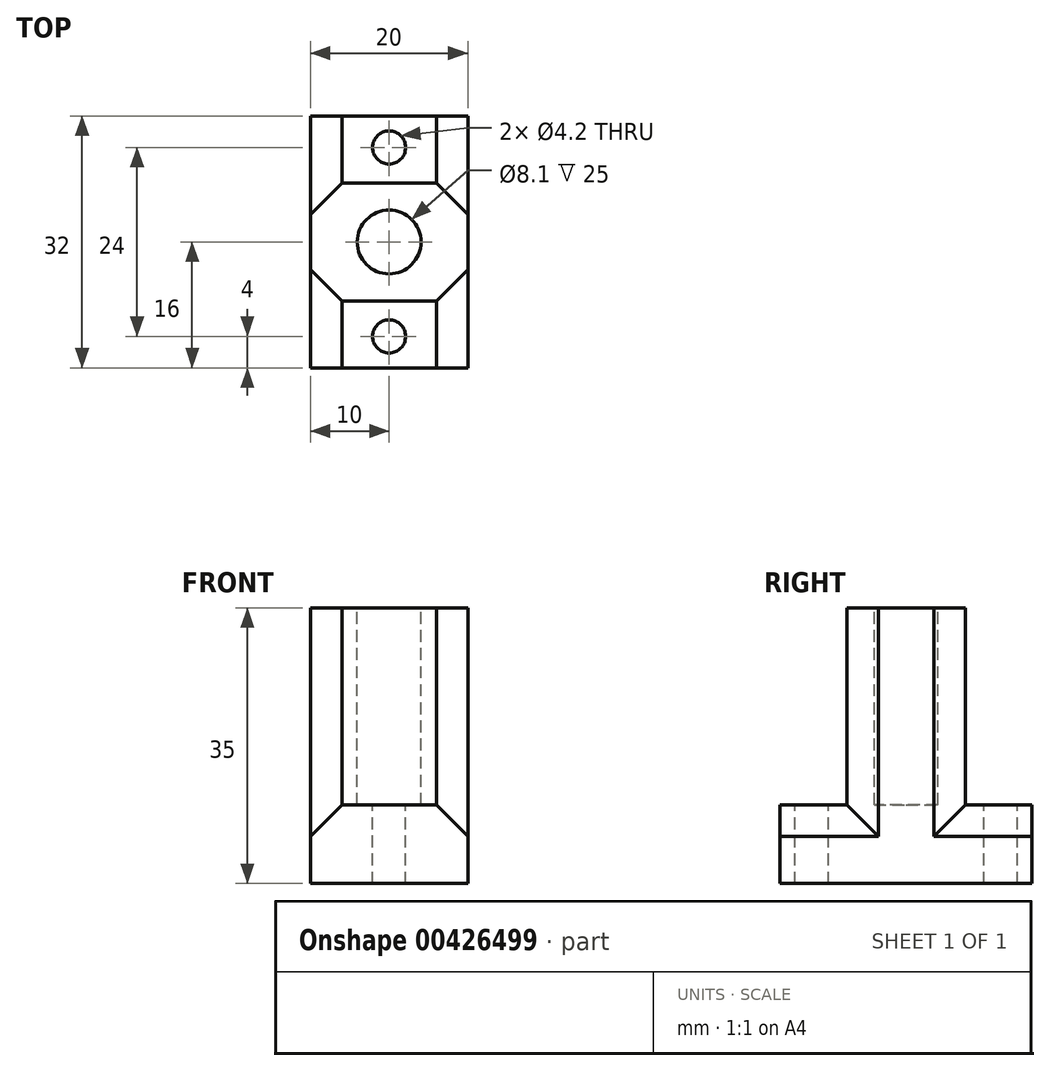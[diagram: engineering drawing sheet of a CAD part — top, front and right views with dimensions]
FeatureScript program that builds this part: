
annotation { "Feature Type Name" : "Feature", "Feature Type Description" : "" }
export const myFeature = defineFeature(function(context is Context, id is Id, definition is map)
    precondition{}
    {
        {
            var Q0;
            Q0=qCreatedBy(makeId("Top.planeOp"),FACE);
            var sketch = newSketch(context, id + "F0", { "sketchPlane" : qUnion([Q0])});
            skLineSegment(sketch, "E0", {"start": v(0, 0) * mm, "end": v(0, 16) * mm, "construction": true});
            skLineSegment(sketch, "E1", {"start": v(0, 0) * mm, "end": v(-10, 0) * mm, "construction": true});
            skLineSegment(sketch, "E2", {"start": v(-10, 0) * mm, "end": v(-10, -16) * mm});
            skLineSegment(sketch, "E3", {"start": v(-10, -16) * mm, "end": v(0, -16) * mm});
            skLineSegment(sketch, "E4", {"start": v(0, -16) * mm, "end": v(0, 0) * mm, "construction": true});
            skLineSegment(sketch, "E5", {"start": v(0, 0) * mm, "end": v(10, 0) * mm, "construction": true});
            skLineSegment(sketch, "E6", {"start": v(10, 0) * mm, "end": v(10, -16) * mm});
            skLineSegment(sketch, "E7", {"start": v(10, -16) * mm, "end": v(0, -16) * mm});
            skLineSegment(sketch, "E8", {"start": v(0, 16) * mm, "end": v(10, 16) * mm});
            skLineSegment(sketch, "E9", {"start": v(10, 16) * mm, "end": v(10, 0) * mm});
            skLineSegment(sketch, "E10", {"start": v(0, 16) * mm, "end": v(-10, 16) * mm});
            skLineSegment(sketch, "E11", {"start": v(-10, 16) * mm, "end": v(-10, 0) * mm});
            skSolve(sketch);
        }
        {
            var Q0;
            Q0 = qSketchRegion(id + "F0", true);
            extrude(context, id + "F1", {"entities" : qUnion([Q0]), "depth" : 10 * mm});
        }
        {
            var Q0;
            Q0=makeQuery(id+"F1.opExtrude","CAP_FACE",FACE,{"disambiguationData":[OSD([sQuery(id+"F0.wireOp",EDGE,"E2"),sQuery(id+"F0.wireOp",EDGE,"E3"),sQuery(id+"F0.wireOp",EDGE,"E6"),sQuery(id+"F0.wireOp",EDGE,"E7"),sQuery(id+"F0.wireOp",EDGE,"E8"),sQuery(id+"F0.wireOp",EDGE,"E9"),sQuery(id+"F0.wireOp",EDGE,"E10"),sQuery(id+"F0.wireOp",EDGE,"E11")])],"isStart":false});
            var sketch = newSketch(context, id + "F2", { "sketchPlane" : qUnion([Q0])});
            skLineSegment(sketch, "E12", {"start": v(0, 0) * mm, "end": v(0, 7.5) * mm, "construction": true});
            skLineSegment(sketch, "E13", {"start": v(0, 7.5) * mm, "end": v(10, 7.5) * mm});
            skLineSegment(sketch, "E14", {"start": v(10, 7.5) * mm, "end": v(10, 0) * mm});
            skLineSegment(sketch, "E15", {"start": v(10, 0) * mm, "end": v(0, 0) * mm, "construction": true});
            skLineSegment(sketch, "E16", {"start": v(0, 0) * mm, "end": v(0, -7.5) * mm, "construction": true});
            skLineSegment(sketch, "E17", {"start": v(0, -7.5) * mm, "end": v(10, -7.5) * mm});
            skLineSegment(sketch, "E18", {"start": v(10, -7.5) * mm, "end": v(10, 0) * mm});
            skLineSegment(sketch, "E19", {"start": v(0, -7.5) * mm, "end": v(-10, -7.5) * mm});
            skLineSegment(sketch, "E20", {"start": v(-10, -7.5) * mm, "end": v(-10, 7.5) * mm});
            skLineSegment(sketch, "E21", {"start": v(-10, 7.5) * mm, "end": v(0, 7.5) * mm});
            skLineSegment(sketch, "E22", {"start": v(0, 0) * mm, "end": v(-10, 0) * mm, "construction": true});
            skSolve(sketch);
        }
        {
            var Q0;
            Q0 = qSketchRegion(id + "F2", true);
            extrude(context, id + "F3", {"entities" : qUnion([Q0]), "operationType" : NewBodyOperationType.ADD, "depth" : 25 * mm});
        }
        {
            var Q0;
            Q0=makeQuery(id+"F3.opExtrude","SWEPT_EDGE",EDGE,{"disambiguationData":[OSD([sQuery(id+"F0.wireOp",EDGE,"E2"),sQuery(id+"F0.wireOp",EDGE,"E11"),sQuery(id+"F2.wireOp",EDGE,"E19"),sQuery(id+"F2.wireOp",EDGE,"E20")])]});
            var Q1;
            Q1=makeQuery(id+"F3.opExtrude","SWEPT_EDGE",EDGE,{"disambiguationData":[OSD([sQuery(id+"F0.wireOp",EDGE,"E6"),sQuery(id+"F0.wireOp",EDGE,"E9"),sQuery(id+"F2.wireOp",EDGE,"E17"),sQuery(id+"F2.wireOp",EDGE,"E18")])]});
            var Q2;
            Q2=makeQuery(id+"F3.opExtrude","SWEPT_EDGE",EDGE,{"disambiguationData":[OSD([sQuery(id+"F0.wireOp",EDGE,"E6"),sQuery(id+"F0.wireOp",EDGE,"E9"),sQuery(id+"F2.wireOp",EDGE,"E13"),sQuery(id+"F2.wireOp",EDGE,"E14")])]});
            var Q3;
            Q3=makeQuery(id+"F3.opExtrude","SWEPT_EDGE",EDGE,{"disambiguationData":[OSD([sQuery(id+"F0.wireOp",EDGE,"E2"),sQuery(id+"F0.wireOp",EDGE,"E11"),sQuery(id+"F2.wireOp",EDGE,"E20"),sQuery(id+"F2.wireOp",EDGE,"E21")])]});
            chamfer(context, id + "F4", {"entities" : qUnion([Q0, Q1, Q2, Q3]), "width" : 4 * mm, "tangentPropagation" : true});
        }
        {
            var Q0;
            {var subQ0=sQuery(id+"F0.wireOp",EDGE,"E10");var subQ1=sQuery(id+"F0.wireOp",EDGE,"E8");var subQ2=sQuery(id+"F0.wireOp",EDGE,"E9");var subQ3=sQuery(id+"F0.wireOp",EDGE,"E6");var subQ4=sQuery(id+"F0.wireOp",EDGE,"E11");var subQ5=sQuery(id+"F0.wireOp",EDGE,"E2");Q0=makeQuery(id+"F3.boolean.opBoolean","SPLIT",FACE,{"disambiguationData":[TD([makeQuery(id+"F1.opExtrude","SWEPT_FACE",FACE,{"disambiguationData":[OSD([subQ1,subQ0])]})])],"derivedFrom":makeQuery(id+"F1.opExtrude","CAP_FACE",FACE,{"disambiguationData":[OSD([subQ5,sQuery(id+"F0.wireOp",EDGE,"E3"),subQ3,sQuery(id+"F0.wireOp",EDGE,"E7"),subQ1,subQ2,subQ0,subQ4])],"isStart":false})});}
            var sketch = newSketch(context, id + "F5", { "sketchPlane" : qUnion([Q0])});
            skCircle(sketch, "E23", {"center": v(0, 12) * mm, "radius": 2.1 * mm});
            skCircle(sketch, "E24", {"center": v(0, -12) * mm, "radius": 2.1 * mm});
            skSolve(sketch);
        }
        {
            var Q0;
            Q0 = qSketchRegion(id + "F5", true);
            extrude(context, id + "F6", {"entities" : qUnion([Q0]), "operationType" : NewBodyOperationType.REMOVE, "endBound" : BoundingType.THROUGH_ALL, "oppositeDirection" : true, "depth" : 25 * mm});
        }
        {
            var Q0;
            Q0=makeQuery(id+"F3.opExtrude","CAP_FACE",FACE,{"disambiguationData":[OSD([sQuery(id+"F2.wireOp",EDGE,"E13"),sQuery(id+"F2.wireOp",EDGE,"E14"),sQuery(id+"F2.wireOp",EDGE,"E17"),sQuery(id+"F2.wireOp",EDGE,"E18"),sQuery(id+"F2.wireOp",EDGE,"E19"),sQuery(id+"F2.wireOp",EDGE,"E20"),sQuery(id+"F2.wireOp",EDGE,"E21")])],"isStart":false});
            var sketch = newSketch(context, id + "F7", { "sketchPlane" : qUnion([Q0])});
            skCircle(sketch, "E25", {"center": v(0, 0) * mm, "radius": 4.05 * mm});
            skSolve(sketch);
        }
        {
            var Q0;
            Q0 = qSketchRegion(id + "F7", true);
            extrude(context, id + "F8", {"entities" : qUnion([Q0]), "operationType" : NewBodyOperationType.REMOVE, "oppositeDirection" : true, "depth" : 25 * mm});
        }
        {
            var Q0;
            {var subQ0=sQuery(id+"F0.wireOp",EDGE,"E10");var subQ1=sQuery(id+"F0.wireOp",EDGE,"E8");var subQ2=sQuery(id+"F0.wireOp",EDGE,"E11");var subQ3=sQuery(id+"F0.wireOp",EDGE,"E2");Q0=makeQuery(id+"F3.boolean.opBoolean","SPLIT",EDGE,{"disambiguationData":[TD([makeQuery(id+"F1.opExtrude","SWEPT_FACE",FACE,{"disambiguationData":[OSD([subQ1,subQ0])]})])],"derivedFrom":makeQuery(id+"F1.opExtrude","CAP_EDGE",EDGE,{"disambiguationData":[OSD([subQ3,subQ2])],"isStart":false})});}
            var Q1;
            {var subQ0=sQuery(id+"F0.wireOp",EDGE,"E7");var subQ1=sQuery(id+"F0.wireOp",EDGE,"E3");var subQ2=sQuery(id+"F0.wireOp",EDGE,"E11");var subQ3=sQuery(id+"F0.wireOp",EDGE,"E2");Q1=makeQuery(id+"F3.boolean.opBoolean","SPLIT",EDGE,{"disambiguationData":[TD([makeQuery(id+"F1.opExtrude","SWEPT_FACE",FACE,{"disambiguationData":[OSD([subQ1,subQ0])]})])],"derivedFrom":makeQuery(id+"F1.opExtrude","CAP_EDGE",EDGE,{"disambiguationData":[OSD([subQ3,subQ2])],"isStart":false})});}
            var Q2;
            {var subQ0=sQuery(id+"F0.wireOp",EDGE,"E9");var subQ1=sQuery(id+"F0.wireOp",EDGE,"E6");var subQ2=sQuery(id+"F0.wireOp",EDGE,"E7");var subQ3=sQuery(id+"F0.wireOp",EDGE,"E3");Q2=makeQuery(id+"F3.boolean.opBoolean","SPLIT",EDGE,{"disambiguationData":[TD([makeQuery(id+"F1.opExtrude","SWEPT_FACE",FACE,{"disambiguationData":[OSD([subQ3,subQ2])]})])],"derivedFrom":makeQuery(id+"F1.opExtrude","CAP_EDGE",EDGE,{"disambiguationData":[OSD([subQ1,subQ0])],"isStart":false})});}
            var Q3;
            {var subQ0=sQuery(id+"F0.wireOp",EDGE,"E10");var subQ1=sQuery(id+"F0.wireOp",EDGE,"E8");var subQ2=sQuery(id+"F0.wireOp",EDGE,"E9");var subQ3=sQuery(id+"F0.wireOp",EDGE,"E6");Q3=makeQuery(id+"F3.boolean.opBoolean","SPLIT",EDGE,{"disambiguationData":[TD([makeQuery(id+"F1.opExtrude","SWEPT_FACE",FACE,{"disambiguationData":[OSD([subQ1,subQ0])]})])],"derivedFrom":makeQuery(id+"F1.opExtrude","CAP_EDGE",EDGE,{"disambiguationData":[OSD([subQ3,subQ2])],"isStart":false})});}
            chamfer(context, id + "F9", {"entities" : qUnion([Q0, Q1, Q2, Q3]), "width" : 4 * mm, "tangentPropagation" : true});
        }
    });
